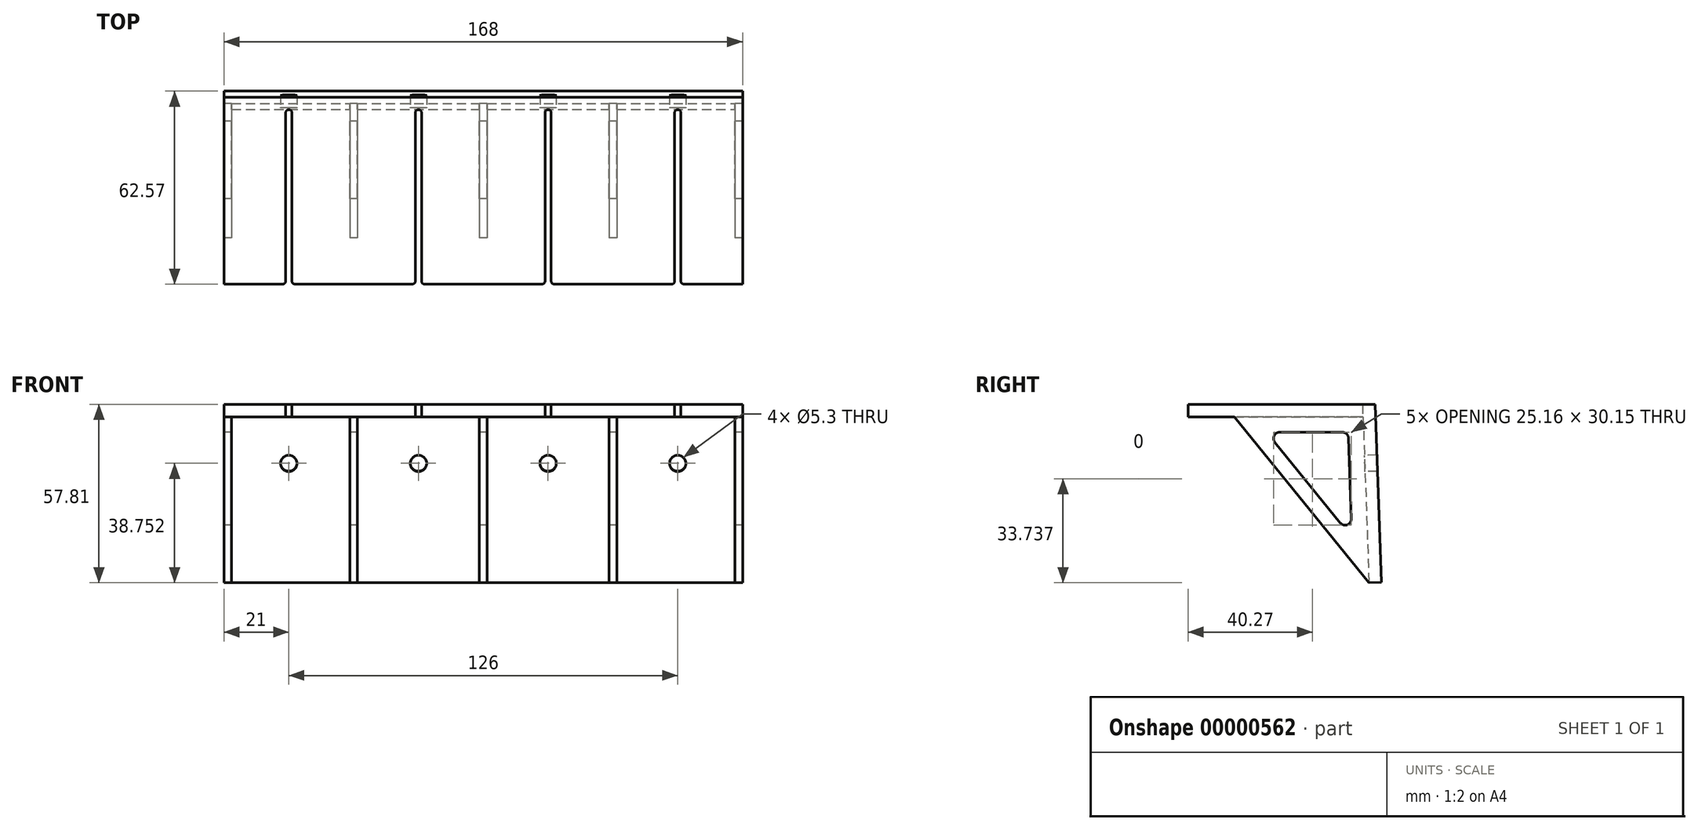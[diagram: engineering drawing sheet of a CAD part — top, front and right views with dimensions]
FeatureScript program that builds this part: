
annotation { "Feature Type Name" : "Feature", "Feature Type Description" : "" }
export const myFeature = defineFeature(function(context is Context, id is Id, definition is map)
    precondition{}
    {
        {
            var Q0;
            Q0=qCreatedBy(makeId("Top.planeOp"),FACE);
            var sketch = newSketch(context, id + "F0", { "sketchPlane" : qUnion([Q0])});
            skLineSegment(sketch, "E0", {"start": v(0, 0) * mm, "end": v(168, 0) * mm});
            skLineSegment(sketch, "E1", {"start": v(0, 0) * mm, "end": v(0, -60.56) * mm});
            skLineSegment(sketch, "E2", {"start": v(0, -60.56) * mm, "end": v(19, -60.56) * mm});
            skLineSegment(sketch, "E3", {"start": v(20, -59.56) * mm, "end": v(20, -5) * mm});
            skLineSegment(sketch, "E4", {"start": v(22, -5) * mm, "end": v(22, -59.56) * mm});
            skLineSegment(sketch, "E5", {"start": v(23, -60.56) * mm, "end": v(61, -60.56) * mm});
            skLineSegment(sketch, "E6", {"start": v(62, -59.56) * mm, "end": v(62, -5) * mm});
            skLineSegment(sketch, "E7", {"start": v(64, -5) * mm, "end": v(64, -59.56) * mm});
            skLineSegment(sketch, "E8", {"start": v(65, -60.56) * mm, "end": v(103, -60.56) * mm});
            skLineSegment(sketch, "E9", {"start": v(104, -59.56) * mm, "end": v(104, -5) * mm});
            skLineSegment(sketch, "E10", {"start": v(106, -5) * mm, "end": v(106, -59.56) * mm});
            skLineSegment(sketch, "E11", {"start": v(107, -60.56) * mm, "end": v(145, -60.56) * mm});
            skLineSegment(sketch, "E12", {"start": v(146, -59.56) * mm, "end": v(146, -5) * mm});
            skLineSegment(sketch, "E13", {"start": v(148, -5) * mm, "end": v(148, -59.56) * mm});
            skArc(sketch, "E14", {"start": v(20, -5) * mm, "mid": v(21, -4) * mm, "end": v(22, -5) * mm});
            skArc(sketch, "E15", {"start": v(62, -5) * mm, "mid": v(63, -4) * mm, "end": v(64, -5) * mm});
            skArc(sketch, "E16", {"start": v(104, -5) * mm, "mid": v(105, -4) * mm, "end": v(106, -5) * mm});
            skArc(sketch, "E17", {"start": v(146, -5) * mm, "mid": v(147, -4) * mm, "end": v(148, -5) * mm});
            skLineSegment(sketch, "E18", {"start": v(21, -5) * mm, "end": v(147, -5) * mm, "construction": true});
            skPoint(sketch, "E19.visualSharp", {"position": v(62, -60.56) * mm});
            skArc(sketch, "E19.filletArc", {"start": v(61, -60.56) * mm, "mid": v(61.7, -60.27) * mm, "end": v(62, -59.56) * mm});
            skPoint(sketch, "E20.visualSharp", {"position": v(20, -60.56) * mm});
            skArc(sketch, "E20.filletArc", {"start": v(19, -60.56) * mm, "mid": v(19.7, -60.27) * mm, "end": v(20, -59.56) * mm});
            skPoint(sketch, "E21.visualSharp", {"position": v(22, -60.56) * mm});
            skArc(sketch, "E21.filletArc", {"start": v(22, -59.56) * mm, "mid": v(22.3, -60.27) * mm, "end": v(23, -60.56) * mm});
            skPoint(sketch, "E22.visualSharp", {"position": v(64, -60.56) * mm});
            skArc(sketch, "E22.filletArc", {"start": v(64, -59.56) * mm, "mid": v(64.3, -60.27) * mm, "end": v(65, -60.56) * mm});
            skPoint(sketch, "E23.visualSharp", {"position": v(104, -60.56) * mm});
            skArc(sketch, "E23.filletArc", {"start": v(103, -60.56) * mm, "mid": v(103.7, -60.27) * mm, "end": v(104, -59.56) * mm});
            skPoint(sketch, "E24.visualSharp", {"position": v(106, -60.56) * mm});
            skArc(sketch, "E24.filletArc", {"start": v(106, -59.56) * mm, "mid": v(106.3, -60.27) * mm, "end": v(107, -60.56) * mm});
            skPoint(sketch, "E25.visualSharp", {"position": v(146, -60.56) * mm});
            skArc(sketch, "E25.filletArc", {"start": v(145, -60.56) * mm, "mid": v(145.7, -60.27) * mm, "end": v(146, -59.56) * mm});
            skLineSegment(sketch, "E26", {"start": v(149, -60.56) * mm, "end": v(168, -60.56) * mm});
            skLineSegment(sketch, "E27", {"start": v(168, -60.56) * mm, "end": v(168, 0) * mm});
            skPoint(sketch, "E28.visualSharp", {"position": v(148, -60.56) * mm});
            skArc(sketch, "E28.filletArc", {"start": v(148, -59.56) * mm, "mid": v(148.3, -60.27) * mm, "end": v(149, -60.56) * mm});
            skSolve(sketch);
        }
        {
            var Q0;
            Q0=makeQuery(id+"F0.imprint","IMPRINT",FACE,{"disambiguationData":[TD([[makeQuery(id+"F0.imprint","IMPRINT",EDGE,{"derivedFrom":sQuery(id+"F0.wireOp",EDGE,"E0")}),-1.0]])]});
            extrude(context, id + "F1", {"entities" : qUnion([Q0]), "depth" : 4 * mm});
        }
        {
            var Q0;
            Q0=makeQuery(id+"F1.opExtrude","SWEPT_FACE",FACE,{"disambiguationData":[OSD([sQuery(id+"F0.wireOp",EDGE,"E0")])]});
            var sketch = newSketch(context, id + "F2", { "sketchPlane" : qUnion([Q0])});
            skLineSegment(sketch, "E29", {"start": v(0, 4) * mm, "end": v(0, -100) * mm});
            skLineSegment(sketch, "E30", {"start": v(0, -100) * mm, "end": v(-42, -100) * mm});
            skLineSegment(sketch, "E31", {"start": v(-42, -110) * mm, "end": v(-42, -100) * mm});
            skLineSegment(sketch, "E32", {"start": v(-42, -110) * mm, "end": v(-84, -110) * mm});
            skLineSegment(sketch, "E33", {"start": v(-84, -135) * mm, "end": v(-84, -110) * mm});
            skLineSegment(sketch, "E34", {"start": v(-84, -135) * mm, "end": v(-126, -135) * mm});
            skLineSegment(sketch, "E35", {"start": v(-126, -155) * mm, "end": v(-126, -135) * mm});
            skLineSegment(sketch, "E36", {"start": v(-126, -155) * mm, "end": v(-168, -155) * mm});
            skLineSegment(sketch, "E37", {"start": v(-168, -155) * mm, "end": v(-168, -22) * mm});
            skLineSegment(sketch, "E38", {"start": v(-147, 4) * mm, "end": v(-147, -155) * mm, "construction": true});
            skLineSegment(sketch, "E39", {"start": v(-105, -135) * mm, "end": v(-105, 4) * mm, "construction": true});
            skLineSegment(sketch, "E40", {"start": v(-63, -110) * mm, "end": v(-63, 4) * mm, "construction": true});
            skLineSegment(sketch, "E41", {"start": v(-21, -100) * mm, "end": v(-21, 4) * mm, "construction": true});
            skLineSegment(sketch, "E42", {"start": v(-21, -48.08) * mm, "end": v(-63, -48.08) * mm, "construction": true});
            skLineSegment(sketch, "E43", {"start": v(-63, -48.08) * mm, "end": v(-105, -48.08) * mm, "construction": true});
            skLineSegment(sketch, "E44", {"start": v(-105, -48.08) * mm, "end": v(-147, -48.08) * mm, "construction": true});
            skLineSegment(sketch, "E45", {"start": v(-126, -135) * mm, "end": v(-126, -48.08) * mm, "construction": true});
            skLineSegment(sketch, "E46", {"start": v(-84, -110) * mm, "end": v(-84, -48.08) * mm, "construction": true});
            skLineSegment(sketch, "E47", {"start": v(-42, -100) * mm, "end": v(-42, -48.08) * mm, "construction": true});
            skLineSegment(sketch, "E48", {"start": v(0, 4) * mm, "end": v(-168, 4) * mm});
            skLineSegment(sketch, "E49", {"start": v(-168, 4) * mm, "end": v(-297, 4) * mm});
            skLineSegment(sketch, "E50", {"start": v(-297, 4) * mm, "end": v(-297, -22) * mm});
            skLineSegment(sketch, "E51", {"start": v(-297, -22) * mm, "end": v(-168, -22) * mm});
            skCircle(sketch, "E52", {"center": v(-188, -9) * mm, "radius": 9 * mm});
            skCircle(sketch, "E53", {"center": v(-236, -9) * mm, "radius": 9 * mm});
            skCircle(sketch, "E54", {"center": v(-284, -9) * mm, "radius": 9 * mm});
            skLineSegment(sketch, "E55", {"start": v(-188, -9) * mm, "end": v(-284, -9) * mm, "construction": true});
            skLineSegment(sketch, "E56", {"start": v(-284, -9) * mm, "end": v(-297, -9) * mm, "construction": true});
            skLineSegment(sketch, "E57", {"start": v(-168, -22) * mm, "end": v(-168, 4) * mm});
            skSolve(sketch);
        }
        {
            var Q0;
            Q0=makeQuery(id+"F1.opExtrude","SWEPT_FACE",FACE,{"disambiguationData":[OSD([sQuery(id+"F0.wireOp",EDGE,"E1")])]});
            var sketch = newSketch(context, id + "F3", { "sketchPlane" : qUnion([Q0])});
            skLineSegment(sketch, "E58", {"start": v(45.56, 0) * mm, "end": v(1.98, -53.81) * mm});
            skLineSegment(sketch, "E59", {"start": v(3.86, 0) * mm, "end": v(45.56, 0) * mm});
            skLineSegment(sketch, "E60.0", {"start": v(7.71, -33.08) * mm, "end": v(8.62, -6.93) * mm});
            skLineSegment(sketch, "E60.1", {"start": v(32.44, -8.26) * mm, "end": v(11.26, -34.4) * mm});
            skLineSegment(sketch, "E60.2", {"start": v(10.62, -5) * mm, "end": v(30.88, -5) * mm});
            skPoint(sketch, "E61.visualSharp", {"position": v(7.5, -39.05) * mm});
            skArc(sketch, "E61.filletArc", {"start": v(7.71, -33.08) * mm, "mid": v(9, -35.02) * mm, "end": v(11.26, -34.4) * mm});
            skPoint(sketch, "E62.visualSharp", {"position": v(8.7, -5) * mm});
            skArc(sketch, "E62.filletArc", {"start": v(10.62, -5) * mm, "mid": v(9.23, -5.56) * mm, "end": v(8.62, -6.93) * mm});
            skPoint(sketch, "E63.visualSharp", {"position": v(35.08, -5) * mm});
            skArc(sketch, "E63.filletArc", {"start": v(32.44, -8.26) * mm, "mid": v(32.69, -6.14) * mm, "end": v(30.88, -5) * mm});
            skLineSegment(sketch, "E64", {"start": v(0, 4) * mm, "end": v(-2.01, -53.67) * mm});
            skLineSegment(sketch, "E65", {"start": v(1.98, -53.81) * mm, "end": v(3.86, 0) * mm});
            skLineSegment(sketch, "E66", {"start": v(0, 4) * mm, "end": v(4, 4) * mm});
            skLineSegment(sketch, "E67", {"start": v(4, 4) * mm, "end": v(3.86, 0) * mm});
            skLineSegment(sketch, "E68", {"start": v(1.98, -53.81) * mm, "end": v(-2.01, -53.67) * mm});
            skSolve(sketch);
        }
        {
            var Q0;
            Q0=makeQuery(id+"F3.imprint","IMPRINT",FACE,{"disambiguationData":[TD([[makeQuery(id+"F3.imprint","IMPRINT",EDGE,{"derivedFrom":sQuery(id+"F3.wireOp",EDGE,"E64")}),1.0]])]});
            var Q1;
            Q1=makeQuery(id+"F3.imprint","IMPRINT",FACE,{"disambiguationData":[TD([[makeQuery(id+"F3.imprint","IMPRINT",EDGE,{"derivedFrom":sQuery(id+"F3.wireOp",EDGE,"E58")}),-1.0]])]});
            var Q2;
            Q2=makeQuery(id+"F1.opExtrude","SWEPT_FACE",FACE,{"disambiguationData":[OSD([sQuery(id+"F0.wireOp",EDGE,"E27")])]});
            extrude(context, id + "F4", {"entities" : qUnion([Q0, Q1]), "operationType" : NewBodyOperationType.ADD, "endBound" : BoundingType.UP_TO_SURFACE, "oppositeDirection" : true, "endBoundEntityFace" : qUnion([Q2]), "depth" : 2.5 * mm});
        }
        {
            var Q0;
            Q0=makeQuery(id+"F4.opExtrude","SWEPT_FACE",FACE,{"disambiguationData":[OSD([sQuery(id+"F3.wireOp",EDGE,"E64")])]});
            cPlane(context, id + "F5", {"entities" : qUnion([Q0]), "cplaneType" : CPlaneType.OFFSET, "offset" : 4 * mm, "oppositeDirection" : true, "width" : 150 * mm, "height" : 150 * mm});
        }
        {
            var Q0;
            Q0=makeQuery(id+"F1.opExtrude","SWEPT_FACE",FACE,{"disambiguationData":[OSD([sQuery(id+"F0.wireOp",EDGE,"E2")])]});
            var sketch = newSketch(context, id + "F6", { "sketchPlane" : qUnion([Q0])});
            skLineSegment(sketch, "E69.bottom", {"start": v(2.5, 0) * mm, "end": v(40.75, 0) * mm});
            skLineSegment(sketch, "E69.top", {"start": v(2.5, -53.81) * mm, "end": v(40.75, -53.81) * mm});
            skLineSegment(sketch, "E69.left", {"start": v(2.5, 0) * mm, "end": v(2.5, -53.81) * mm});
            skLineSegment(sketch, "E69.right", {"start": v(40.75, 0) * mm, "end": v(40.75, -53.81) * mm});
            skLineSegment(sketch, "E70.bottom", {"start": v(43.25, 0) * mm, "end": v(82.75, 0) * mm});
            skLineSegment(sketch, "E70.top", {"start": v(43.25, -53.81) * mm, "end": v(82.75, -53.81) * mm});
            skLineSegment(sketch, "E70.left", {"start": v(43.25, 0) * mm, "end": v(43.25, -53.81) * mm});
            skLineSegment(sketch, "E70.right", {"start": v(82.75, 0) * mm, "end": v(82.75, -53.81) * mm});
            skLineSegment(sketch, "E71.bottom", {"start": v(85.25, 0) * mm, "end": v(124.75, 0) * mm});
            skLineSegment(sketch, "E71.top", {"start": v(85.25, -53.81) * mm, "end": v(124.75, -53.81) * mm});
            skLineSegment(sketch, "E71.left", {"start": v(85.25, 0) * mm, "end": v(85.25, -53.81) * mm});
            skLineSegment(sketch, "E71.right", {"start": v(124.75, 0) * mm, "end": v(124.75, -53.81) * mm});
            skLineSegment(sketch, "E72.bottom", {"start": v(127.25, 0) * mm, "end": v(165.5, 0) * mm});
            skLineSegment(sketch, "E72.top", {"start": v(127.25, -53.81) * mm, "end": v(165.5, -53.81) * mm});
            skLineSegment(sketch, "E72.left", {"start": v(127.25, 0) * mm, "end": v(127.25, -53.81) * mm});
            skLineSegment(sketch, "E72.right", {"start": v(165.5, 0) * mm, "end": v(165.5, -53.81) * mm});
            skLineSegment(sketch, "E73", {"start": v(40.75, -53.81) * mm, "end": v(43.25, -53.81) * mm, "construction": true});
            skLineSegment(sketch, "E74", {"start": v(82.75, -53.81) * mm, "end": v(85.25, -53.81) * mm, "construction": true});
            skLineSegment(sketch, "E75", {"start": v(124.75, -53.81) * mm, "end": v(127.25, -53.81) * mm, "construction": true});
            skLineSegment(sketch, "E76", {"start": v(42, -53.81) * mm, "end": v(42, -100) * mm, "construction": true});
            skSolve(sketch);
        }
        {
            var Q0;
            {Q0=qUnion([makeQuery(id+"F6.imprint","IMPRINT",FACE,{"disambiguationData":[TD([[makeQuery(id+"F6.imprint","IMPRINT",EDGE,{"derivedFrom":sQuery(id+"F6.wireOp",EDGE,"E72.bottom")}),-1.0]])]}),makeQuery(id+"F6.imprint","IMPRINT",FACE,{"disambiguationData":[TD([[makeQuery(id+"F6.imprint","IMPRINT",EDGE,{"derivedFrom":sQuery(id+"F6.wireOp",EDGE,"E71.bottom")}),-1.0]])]}),makeQuery(id+"F6.imprint","IMPRINT",FACE,{"disambiguationData":[TD([[makeQuery(id+"F6.imprint","IMPRINT",EDGE,{"derivedFrom":sQuery(id+"F6.wireOp",EDGE,"E70.bottom")}),-1.0]])]}),makeQuery(id+"F6.imprint","IMPRINT",FACE,{"disambiguationData":[TD([[makeQuery(id+"F6.imprint","IMPRINT",EDGE,{"derivedFrom":sQuery(id+"F6.wireOp",EDGE,"E69.top")}),1.0]])]})]);}
            var Q1;
            Q1=qCreatedBy(id+"F5.planeOp",FACE);
            extrude(context, id + "F7", {"entities" : qUnion([Q0]), "operationType" : NewBodyOperationType.REMOVE, "endBound" : BoundingType.UP_TO_SURFACE, "oppositeDirection" : true, "endBoundEntityFace" : qUnion([Q1]), "depth" : 25 * mm});
        }
        {
            var Q0;
            Q0=makeQuery(id+"F7.boolean.opBoolean","COPY",FACE,{"derivedFrom":makeQuery(id+"F7.opExtrude","CAP_FACE",FACE,{"disambiguationData":[OSD([sQuery(id+"F6.wireOp",EDGE,"E69.bottom"),sQuery(id+"F6.wireOp",EDGE,"E69.top"),sQuery(id+"F6.wireOp",EDGE,"E69.left"),sQuery(id+"F6.wireOp",EDGE,"E69.right")])],"isStart":false})});
            var sketch = newSketch(context, id + "F8", { "sketchPlane" : qUnion([Q0])});
            skCircle(sketch, "E77", {"center": v(21, -15) * mm, "radius": 2.65 * mm});
            skCircle(sketch, "E78", {"center": v(63, -15) * mm, "radius": 2.65 * mm});
            skCircle(sketch, "E79", {"center": v(105, -15) * mm, "radius": 2.65 * mm});
            skCircle(sketch, "E80", {"center": v(147, -15) * mm, "radius": 2.65 * mm});
            skLineSegment(sketch, "E81", {"start": v(147, -15) * mm, "end": v(21, -15) * mm, "construction": true});
            skSolve(sketch);
        }
        {
            var Q0;
            {Q0=qUnion([makeQuery(id+"F8.imprint","IMPRINT",FACE,{"disambiguationData":[TD([[makeQuery(id+"F8.imprint","IMPRINT",EDGE,{"derivedFrom":sQuery(id+"F8.wireOp",EDGE,"E80")}),1.0]])]}),makeQuery(id+"F8.imprint","IMPRINT",FACE,{"disambiguationData":[TD([[makeQuery(id+"F8.imprint","IMPRINT",EDGE,{"derivedFrom":sQuery(id+"F8.wireOp",EDGE,"E79")}),1.0]])]}),makeQuery(id+"F8.imprint","IMPRINT",FACE,{"disambiguationData":[TD([[makeQuery(id+"F8.imprint","IMPRINT",EDGE,{"derivedFrom":sQuery(id+"F8.wireOp",EDGE,"E78")}),1.0]])]}),makeQuery(id+"F8.imprint","IMPRINT",FACE,{"disambiguationData":[TD([[makeQuery(id+"F8.imprint","IMPRINT",EDGE,{"derivedFrom":sQuery(id+"F8.wireOp",EDGE,"E77")}),1.0]])]})]);}
            extrude(context, id + "F9", {"entities" : qUnion([Q0]), "operationType" : NewBodyOperationType.REMOVE, "endBound" : BoundingType.THROUGH_ALL, "oppositeDirection" : true, "depth" : 25 * mm});
        }
    });
